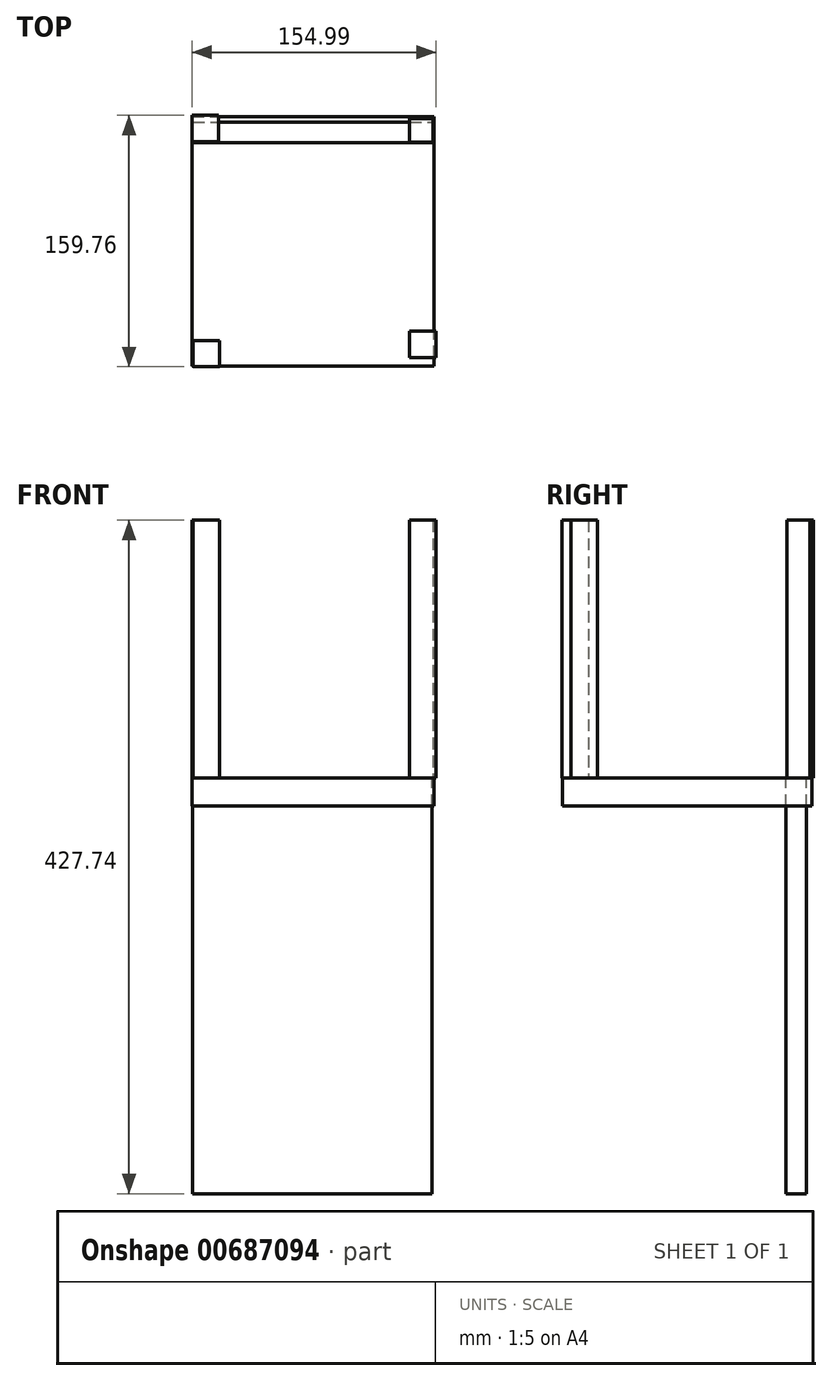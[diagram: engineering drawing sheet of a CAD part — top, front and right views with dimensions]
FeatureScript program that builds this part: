
annotation { "Feature Type Name" : "Feature", "Feature Type Description" : "" }
export const myFeature = defineFeature(function(context is Context, id is Id, definition is map)
    precondition{}
    {
        {
            var Q0;
            Q0=qCreatedBy(makeId("Top.planeOp"),FACE);
            var sketch = newSketch(context, id + "F0", { "sketchPlane" : qUnion([Q0])});
            skLineSegment(sketch, "E0.bottom", {"start": v(-75.95, 78.36) * mm, "end": v(-59.22, 78.36) * mm});
            skLineSegment(sketch, "E0.top", {"start": v(-75.95, 61.62) * mm, "end": v(-59.22, 61.62) * mm});
            skLineSegment(sketch, "E0.left", {"start": v(-75.95, 78.36) * mm, "end": v(-75.95, 61.62) * mm});
            skLineSegment(sketch, "E0.right", {"start": v(-59.22, 78.36) * mm, "end": v(-59.22, 61.62) * mm});
            skLineSegment(sketch, "E1.bottom", {"start": v(76.97, 76.08) * mm, "end": v(62.26, 76.08) * mm});
            skLineSegment(sketch, "E1.top", {"start": v(76.97, 61.37) * mm, "end": v(62.26, 61.37) * mm});
            skLineSegment(sketch, "E1.left", {"start": v(76.97, 76.08) * mm, "end": v(76.97, 61.37) * mm});
            skLineSegment(sketch, "E1.right", {"start": v(62.26, 76.08) * mm, "end": v(62.26, 61.37) * mm});
            skLineSegment(sketch, "E2.bottom", {"start": v(-75.2, -81.4) * mm, "end": v(-58.45, -81.4) * mm});
            skLineSegment(sketch, "E2.top", {"start": v(-75.2, -64.67) * mm, "end": v(-58.45, -64.67) * mm});
            skLineSegment(sketch, "E2.left", {"start": v(-75.2, -81.4) * mm, "end": v(-75.2, -64.67) * mm});
            skLineSegment(sketch, "E2.right", {"start": v(-58.45, -81.4) * mm, "end": v(-58.45, -64.67) * mm});
            skLineSegment(sketch, "E3.bottom", {"start": v(79, -75.57) * mm, "end": v(62.26, -75.57) * mm});
            skLineSegment(sketch, "E3.top", {"start": v(79, -58.83) * mm, "end": v(62.26, -58.83) * mm});
            skLineSegment(sketch, "E3.left", {"start": v(79, -75.57) * mm, "end": v(79, -58.83) * mm});
            skLineSegment(sketch, "E3.right", {"start": v(62.26, -75.57) * mm, "end": v(62.26, -58.83) * mm});
            skSolve(sketch);
        }
        {
            var Q0;
            Q0 = qSketchRegion(id + "F0", true);
            var Q1;
            Q1=makeQuery(id+"F0.imprint","IMPRINT",FACE,{"disambiguationData":[TD([[makeQuery(id+"F0.imprint","IMPRINT",EDGE,{"derivedFrom":sQuery(id+"F0.wireOp",EDGE,"E0.bottom")}),-1.0]])]});
            extrude(context, id + "F1", {"entities" : qUnion([Q0, Q1]), "depth" : 163.58 * mm, "offsetDistance" : 25.4 * mm});
        }
        {
            var Q0;
            Q0=qCreatedBy(makeId("Top.planeOp"),FACE);
            var sketch = newSketch(context, id + "F2", { "sketchPlane" : qUnion([Q0])});
            skLineSegment(sketch, "E4.bottom", {"start": v(-75.99, -81.12) * mm, "end": v(77.7, -81.12) * mm});
            skLineSegment(sketch, "E4.top", {"start": v(-75.99, 77.4) * mm, "end": v(77.7, 77.4) * mm});
            skLineSegment(sketch, "E4.left", {"start": v(-75.99, -81.12) * mm, "end": v(-75.99, 77.4) * mm});
            skLineSegment(sketch, "E4.right", {"start": v(77.7, -81.12) * mm, "end": v(77.7, 77.4) * mm});
            skSolve(sketch);
        }
        {
            var Q0;
            Q0 = qSketchRegion(id + "F2", true);
            extrude(context, id + "F3", {"entities" : qUnion([Q0]), "oppositeDirection" : true, "depth" : 18.03 * mm, "offsetDistance" : 25.4 * mm});
        }
        {
            var Q0;
            Q0=qCreatedBy(makeId("Top.planeOp"),FACE);
            var sketch = newSketch(context, id + "F4", { "sketchPlane" : qUnion([Q0])});
            skLineSegment(sketch, "E5.bottom", {"start": v(-75.64, 73.8) * mm, "end": v(76.42, 73.8) * mm});
            skLineSegment(sketch, "E5.top", {"start": v(-75.64, 60.78) * mm, "end": v(76.42, 60.78) * mm});
            skLineSegment(sketch, "E5.left", {"start": v(-75.64, 73.8) * mm, "end": v(-75.64, 60.78) * mm});
            skLineSegment(sketch, "E5.right", {"start": v(76.42, 73.8) * mm, "end": v(76.42, 60.78) * mm});
            skSolve(sketch);
        }
        {
            var Q0;
            Q0 = qSketchRegion(id + "F4", true);
            extrude(context, id + "F5", {"entities" : qUnion([Q0]), "oppositeDirection" : true, "depth" : 264.16 * mm, "offsetDistance" : 25.4 * mm});
        }
    });
